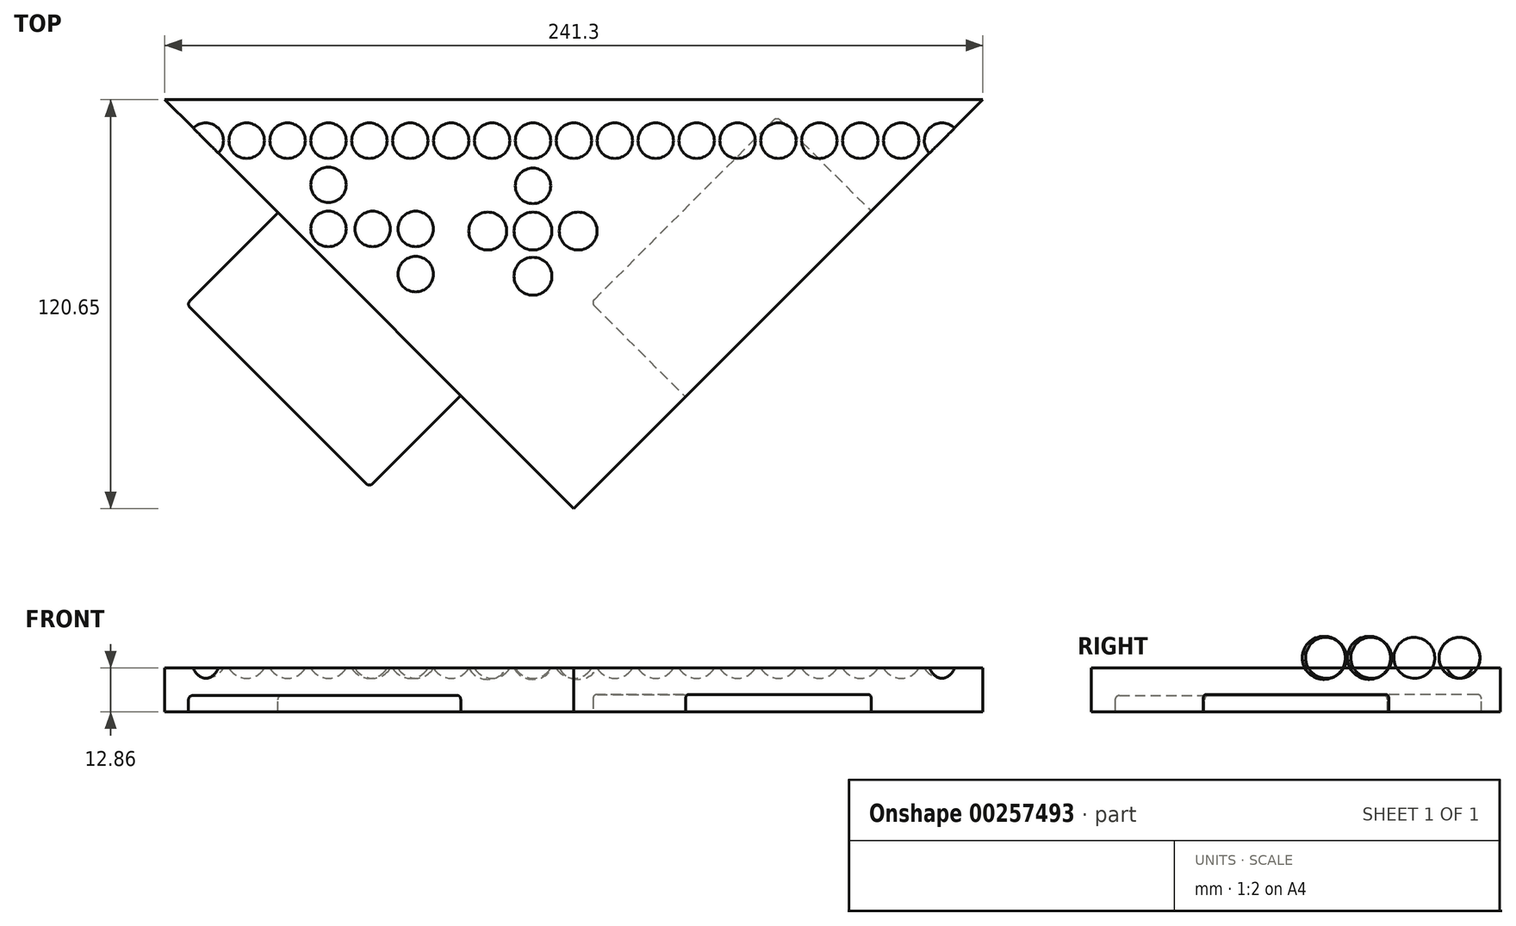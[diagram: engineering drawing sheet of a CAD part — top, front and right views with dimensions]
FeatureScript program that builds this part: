
annotation { "Feature Type Name" : "Feature", "Feature Type Description" : "" }
export const myFeature = defineFeature(function(context is Context, id is Id, definition is map)
    precondition{}
    {
        {
            var Q0;
            Q0=qCreatedBy(makeId("Top.planeOp"),FACE);
            var sketch = newSketch(context, id + "F0", { "sketchPlane" : qUnion([Q0])});
            skLineSegment(sketch, "E0.bottom", {"start": v(120.65, -120.65) * mm, "end": v(-120.65, -120.65) * mm});
            skLineSegment(sketch, "E0.top", {"start": v(120.65, 120.65) * mm, "end": v(-120.65, 120.65) * mm});
            skLineSegment(sketch, "E0.left", {"start": v(120.65, -120.65) * mm, "end": v(120.65, 120.65) * mm});
            skLineSegment(sketch, "E0.right", {"start": v(-120.65, -120.65) * mm, "end": v(-120.65, 120.65) * mm});
            skPoint(sketch, "E0.middle", {"position": v(0, 0) * mm});
            skSolve(sketch);
        }
        {
            var Q0;
            Q0=makeQuery(id+"F0.imprint","IMPRINT",FACE,{"disambiguationData":[TD([[makeQuery(id+"F0.imprint","IMPRINT",EDGE,{"derivedFrom":sQuery(id+"F0.wireOp",EDGE,"E0.bottom")}),-1.0]])]});
            extrude(context, id + "F1", {"entities" : qUnion([Q0]), "offsetDistance" : 25.4 * mm, "depth" : 12.7 * mm});
        }
        {
            var Q0;
            Q0=makeQuery(id+"F1.opExtrude","CAP_FACE",FACE,{"disambiguationData":[OSD([sQuery(id+"F0.wireOp",EDGE,"E0.bottom"),sQuery(id+"F0.wireOp",EDGE,"E0.top"),sQuery(id+"F0.wireOp",EDGE,"E0.left"),sQuery(id+"F0.wireOp",EDGE,"E0.right")])],"isStart":false});
            var sketch = newSketch(context, id + "F2", { "sketchPlane" : qUnion([Q0])});
            skLineSegment(sketch, "E1", {"start": v(120.65, 120.65) * mm, "end": v(0, 0) * mm});
            skLineSegment(sketch, "E2", {"start": v(0, 0) * mm, "end": v(-120.65, 120.65) * mm});
            skLineSegment(sketch, "E3", {"start": v(-120.65, 120.65) * mm, "end": v(-120.65, -120.65) * mm});
            skLineSegment(sketch, "E4", {"start": v(-120.65, -120.65) * mm, "end": v(120.65, -120.65) * mm});
            skLineSegment(sketch, "E5", {"start": v(120.65, -120.65) * mm, "end": v(120.65, 120.65) * mm});
            skSolve(sketch);
        }
        {
            var Q0;
            Q0 = qSketchRegion(id + "F2", true);
            extrude(context, id + "F3", {"entities" : qUnion([Q0]), "operationType" : NewBodyOperationType.REMOVE, "endBound" : BoundingType.THROUGH_ALL, "oppositeDirection" : true, "depth" : 25.4 * mm});
        }
        {
            var Q0;
            Q0=makeQuery(id+"F3.boolean.opBoolean","COPY",FACE,{"derivedFrom":makeQuery(id+"F3.opExtrude","SWEPT_FACE",FACE,{"disambiguationData":[OSD([sQuery(id+"F2.wireOp",EDGE,"E1")])]})});
            var sketch = newSketch(context, id + "F4", { "sketchPlane" : qUnion([Q0])});
            skLineSegment(sketch, "E6.bottom", {"start": v(124.05, 5.08) * mm, "end": v(46.58, 5.08) * mm});
            skLineSegment(sketch, "E6.top", {"start": v(124.05, -5.08) * mm, "end": v(46.58, -5.08) * mm});
            skLineSegment(sketch, "E6.left", {"start": v(124.05, 5.08) * mm, "end": v(124.05, -5.08) * mm});
            skLineSegment(sketch, "E6.right", {"start": v(46.58, 5.08) * mm, "end": v(46.58, -5.08) * mm});
            skPoint(sketch, "E6.middle", {"position": v(85.31, 0) * mm});
            skSolve(sketch);
        }
        {
            var Q0;
            Q0 = qSketchRegion(id + "F4", true);
            extrude(context, id + "F5", {"entities" : qUnion([Q0]), "operationType" : NewBodyOperationType.REMOVE, "oppositeDirection" : true, "depth" : 39.37 * mm});
        }
        {
            var Q0;
            Q0=makeQuery(id+"F3.boolean.opBoolean","COPY",FACE,{"derivedFrom":makeQuery(id+"F3.opExtrude","SWEPT_FACE",FACE,{"disambiguationData":[OSD([sQuery(id+"F2.wireOp",EDGE,"E2")])]})});
            var sketch = newSketch(context, id + "F6", { "sketchPlane" : qUnion([Q0])});
            skLineSegment(sketch, "E7.bottom", {"start": v(-47.21, -4.76) * mm, "end": v(-123.41, -4.76) * mm});
            skLineSegment(sketch, "E7.top", {"start": v(-47.21, 4.76) * mm, "end": v(-123.41, 4.76) * mm});
            skLineSegment(sketch, "E7.left", {"start": v(-47.21, -4.76) * mm, "end": v(-47.21, 4.76) * mm});
            skLineSegment(sketch, "E7.right", {"start": v(-123.41, -4.76) * mm, "end": v(-123.41, 4.76) * mm});
            skPoint(sketch, "E7.middle", {"position": v(-85.31, 0) * mm});
            skSolve(sketch);
        }
        {
            var Q0;
            {var subQ0=sQuery(id+"F6.wireOp",EDGE,"E7.top");Q0=makeQuery(id+"F6.imprint","IMPRINT",FACE,{"disambiguationData":[TD([[makeQuery(id+"F6.imprint","IMPRINT",EDGE,{"derivedFrom":subQ0}),1.0]])]});}
            extrude(context, id + "F7", {"entities" : qUnion([Q0]), "operationType" : NewBodyOperationType.ADD, "depth" : 38.1 * mm});
        }
        {
            var Q0;
            Q0=makeQuery(id+"F7.opExtrude","CAP_EDGE",EDGE,{"disambiguationData":[OSD([sQuery(id+"F6.wireOp",EDGE,"E7.left")])],"isStart":true});
            var Q1;
            Q1=makeQuery(id+"F7.opExtrude","CAP_EDGE",EDGE,{"disambiguationData":[OSD([sQuery(id+"F6.wireOp",EDGE,"E7.top")])],"isStart":true});
            var Q2;
            Q2=makeQuery(id+"F7.opExtrude","CAP_EDGE",EDGE,{"disambiguationData":[OSD([sQuery(id+"F6.wireOp",EDGE,"E7.right")])],"isStart":true});
            var Q3;
            Q3=makeQuery(id+"F5.boolean.opBoolean","COPY",EDGE,{"derivedFrom":makeQuery(id+"F5.opExtrude","CAP_EDGE",EDGE,{"disambiguationData":[OSD([sQuery(id+"F4.wireOp",EDGE,"E6.right")])],"isStart":false})});
            var Q4;
            Q4=makeQuery(id+"F5.boolean.opBoolean","COPY",EDGE,{"derivedFrom":makeQuery(id+"F5.opExtrude","CAP_EDGE",EDGE,{"disambiguationData":[OSD([sQuery(id+"F4.wireOp",EDGE,"E6.bottom")])],"isStart":false})});
            var Q5;
            Q5=makeQuery(id+"F5.boolean.opBoolean","COPY",EDGE,{"derivedFrom":makeQuery(id+"F5.opExtrude","CAP_EDGE",EDGE,{"disambiguationData":[OSD([sQuery(id+"F4.wireOp",EDGE,"E6.left")])],"isStart":false})});
            var Q6;
            Q6=makeQuery(id+"F5.boolean.opBoolean","COPY",EDGE,{"derivedFrom":makeQuery(id+"F5.opExtrude","SWEPT_EDGE",EDGE,{"disambiguationData":[OSD([sQuery(id+"F4.wireOp",EDGE,"E6.bottom"),sQuery(id+"F4.wireOp",EDGE,"E6.left")])]})});
            var Q7;
            Q7=makeQuery(id+"F5.boolean.opBoolean","COPY",EDGE,{"derivedFrom":makeQuery(id+"F5.opExtrude","SWEPT_EDGE",EDGE,{"disambiguationData":[OSD([sQuery(id+"F4.wireOp",EDGE,"E6.bottom"),sQuery(id+"F4.wireOp",EDGE,"E6.right")])]})});
            fillet(context, id + "F8", {"entities" : qUnion([Q0, Q1, Q2, Q3, Q4, Q5, Q6, Q7]), "radius" : 1.27 * mm, "tangentPropagation" : true, "allowEdgeOverflow" : false});
        }
        {
            var Q0;
            Q0=makeQuery(id+"F7.opExtrude","SWEPT_EDGE",EDGE,{"disambiguationData":[OSD([sQuery(id+"F6.wireOp",EDGE,"E7.top"),sQuery(id+"F6.wireOp",EDGE,"E7.left")])]});
            var Q1;
            Q1=makeQuery(id+"F7.opExtrude","CAP_EDGE",EDGE,{"disambiguationData":[OSD([sQuery(id+"F6.wireOp",EDGE,"E7.left")])],"isStart":false});
            var Q2;
            Q2=makeQuery(id+"F7.opExtrude","CAP_EDGE",EDGE,{"disambiguationData":[OSD([sQuery(id+"F6.wireOp",EDGE,"E7.top")])],"isStart":false});
            var Q3;
            Q3=makeQuery(id+"F7.opExtrude","CAP_EDGE",EDGE,{"disambiguationData":[OSD([sQuery(id+"F6.wireOp",EDGE,"E7.right")])],"isStart":false});
            var Q4;
            Q4=makeQuery(id+"F7.opExtrude","SWEPT_EDGE",EDGE,{"disambiguationData":[OSD([sQuery(id+"F6.wireOp",EDGE,"E7.top"),sQuery(id+"F6.wireOp",EDGE,"E7.right")])]});
            var Q5;
            Q5=makeQuery(id+"F5.boolean.opBoolean","COPY",EDGE,{"derivedFrom":makeQuery(id+"F5.opExtrude","CAP_EDGE",EDGE,{"disambiguationData":[OSD([sQuery(id+"F4.wireOp",EDGE,"E6.left")])],"isStart":true})});
            fillet(context, id + "F9", {"entities" : qUnion([Q0, Q1, Q2, Q3, Q4, Q5]), "radius" : 1.27 * mm, "tangentPropagation" : true, "allowEdgeOverflow" : false});
        }
        {
            var Q0;
            Q0=makeQuery(id+"F1.opExtrude","CAP_FACE",FACE,{"disambiguationData":[OSD([sQuery(id+"F0.wireOp",EDGE,"E0.bottom"),sQuery(id+"F0.wireOp",EDGE,"E0.top"),sQuery(id+"F0.wireOp",EDGE,"E0.left"),sQuery(id+"F0.wireOp",EDGE,"E0.right")])],"isStart":false});
            var sketch = newSketch(context, id + "F10", { "sketchPlane" : qUnion([Q0])});
            skLineSegment(sketch, "E8", {"start": v(-120.65, 120.65) * mm, "end": v(120.65, 120.65) * mm});
            skLineSegment(sketch, "E9", {"start": v(120.65, 120.65) * mm, "end": v(0, 0) * mm});
            skLineSegment(sketch, "E10", {"start": v(0, 0) * mm, "end": v(-120.65, 120.65) * mm});
            skSolve(sketch);
        }
        {
            var Q0;
            Q0 = qSketchRegion(id + "F10", true);
            extrude(context, id + "F11", {"entities" : qUnion([Q0]), "operationType" : NewBodyOperationType.ADD, "depth" : 3.17 * mm});
        }
        {
            var Q0;
            Q0=makeQuery(id+"F11.opExtrude","CAP_FACE",FACE,{"disambiguationData":[OSD([sQuery(id+"F10.wireOp",EDGE,"E8"),sQuery(id+"F10.wireOp",EDGE,"E9"),sQuery(id+"F10.wireOp",EDGE,"E10")])],"isStart":false});
            var sketch = newSketch(context, id + "F12", { "sketchPlane" : qUnion([Q0])});
            skCircle(sketch, "E11", {"center": v(0, 111.12) * mm, "radius": 6.35 * mm});
            skSolve(sketch);
        }
        {
            var Q0;
            Q0=makeQuery(id+"F12.imprint","IMPRINT",FACE,{"disambiguationData":[TD([[makeQuery(id+"F12.imprint","IMPRINT",EDGE,{"derivedFrom":sQuery(id+"F12.wireOp",EDGE,"E11")}),-1.0]])]});
            var sketch = newSketch(context, id + "F13", { "sketchPlane" : qUnion([Q0])});
            skLineSegment(sketch, "E12", {"start": v(0, 120.94) * mm, "end": v(0, 0) * mm});
            skSolve(sketch);
        }
        {
            var Q0;
            {var subQ0=makeQuery(id+"F12.imprint","IMPRINT",EDGE,{"derivedFrom":makeQuery(id+"F11.opExtrude","CAP_EDGE",EDGE,{"disambiguationData":[OSD([sQuery(id+"F10.wireOp",EDGE,"E9")])],"isStart":false})});Q0=makeQuery(id+"F13.imprint","IMPRINT",FACE,{"disambiguationData":[TD([[makeQuery(id+"F13.imprint","IMPRINT",EDGE,{"derivedFrom":subQ0}),-1.0]])]});}
            var sketch = newSketch(context, id + "F14", { "sketchPlane" : qUnion([Q0])});
            skArc(sketch, "E13", {"start": v(0, 114.59) * mm, "mid": v(6.03, 108.56) * mm, "end": v(0, 102.52) * mm});
            skLineSegment(sketch, "E14", {"start": v(0, 114.59) * mm, "end": v(0, 102.52) * mm});
            skSolve(sketch);
        }
        {
            var Q0;
            Q0 = qSketchRegion(id + "F14", true);
            var Q1;
            Q1=sQuery(id+"F14.wireOp",EDGE,"E14");
            revolve(context, id + "F15", {"operationType" : NewBodyOperationType.REMOVE, "entities" : qUnion([Q0]), "axis" : qUnion([Q1]), "revolveType" : RevolveType.FULL, "oppositeDirection" : true});
        }
        {
            var Q0;
            Q0=makeQuery(id+"F11.opExtrude","CAP_FACE",FACE,{"disambiguationData":[OSD([sQuery(id+"F10.wireOp",EDGE,"E8"),sQuery(id+"F10.wireOp",EDGE,"E9"),sQuery(id+"F10.wireOp",EDGE,"E10")])],"isStart":false});
            var sketch = newSketch(context, id + "F16", { "sketchPlane" : qUnion([Q0])});
            skLineSegment(sketch, "E15", {"start": v(0, 108.56) * mm, "end": v(-6.03, 108.56) * mm});
            skLineSegment(sketch, "E16", {"start": v(-6.03, 108.56) * mm, "end": v(-18.1, 108.56) * mm});
            skArc(sketch, "E17", {"start": v(-18.1, 108.56) * mm, "mid": v(-12.07, 114.59) * mm, "end": v(-6.03, 108.56) * mm});
            skSolve(sketch);
        }
        {
            var Q0;
            Q0=makeQuery(id+"F16.imprint","IMPRINT",FACE,{"disambiguationData":[TD([[makeQuery(id+"F16.imprint","IMPRINT",EDGE,{"derivedFrom":sQuery(id+"F16.wireOp",EDGE,"E16")}),-1.0]])]});
            var Q1;
            Q1=sQuery(id+"F16.wireOp",EDGE,"E16");
            revolve(context, id + "F17", {"operationType" : NewBodyOperationType.REMOVE, "entities" : qUnion([Q0]), "axis" : qUnion([Q1]), "revolveType" : RevolveType.FULL, "oppositeDirection" : true});
        }
        {
            var Q0;
            Q0=makeQuery(id+"F11.opExtrude","CAP_FACE",FACE,{"disambiguationData":[OSD([sQuery(id+"F10.wireOp",EDGE,"E8"),sQuery(id+"F10.wireOp",EDGE,"E9"),sQuery(id+"F10.wireOp",EDGE,"E10")])],"isStart":false});
            var sketch = newSketch(context, id + "F18", { "sketchPlane" : qUnion([Q0])});
            skLineSegment(sketch, "E18", {"start": v(-11.75, 108.56) * mm, "end": v(-18.1, 108.56) * mm});
            skLineSegment(sketch, "E19", {"start": v(-18.1, 108.56) * mm, "end": v(-30.16, 108.56) * mm});
            skArc(sketch, "E20", {"start": v(-30.16, 108.56) * mm, "mid": v(-24.13, 114.59) * mm, "end": v(-18.1, 108.56) * mm});
            skSolve(sketch);
        }
        {
            var Q0;
            Q0=makeQuery(id+"F16.imprint","IMPRINT",FACE,{"disambiguationData":[TD([[makeQuery(id+"F16.imprint","IMPRINT",EDGE,{"derivedFrom":sQuery(id+"F16.wireOp",EDGE,"E16")}),1.0]])]});
            var sketch = newSketch(context, id + "F19", { "sketchPlane" : qUnion([Q0])});
            skLineSegment(sketch, "E21", {"start": v(-30.16, 108.56) * mm, "end": v(-42.23, 108.56) * mm});
            skArc(sketch, "E22", {"start": v(-42.23, 108.56) * mm, "mid": v(-36.2, 114.59) * mm, "end": v(-30.16, 108.56) * mm});
            skSolve(sketch);
        }
        {
            var Q0;
            Q0 = qSketchRegion(id + "F18", true);
            var Q1;
            Q1 = qSketchRegion(id + "F19", true);
            var Q2;
            Q2=sQuery(id+"F19.wireOp",EDGE,"E21");
            revolve(context, id + "F20", {"operationType" : NewBodyOperationType.REMOVE, "entities" : qUnion([Q0, Q1]), "axis" : qUnion([Q2]), "revolveType" : RevolveType.FULL, "oppositeDirection" : true});
        }
        {
            var Q0;
            Q0=makeQuery(id+"F16.imprint","IMPRINT",FACE,{"disambiguationData":[TD([[makeQuery(id+"F16.imprint","IMPRINT",EDGE,{"derivedFrom":sQuery(id+"F16.wireOp",EDGE,"E16")}),1.0]])]});
            var sketch = newSketch(context, id + "F21", { "sketchPlane" : qUnion([Q0])});
            skLineSegment(sketch, "E23", {"start": v(-42.23, 108.56) * mm, "end": v(-54.3, 108.56) * mm});
            skArc(sketch, "E24", {"start": v(-54.3, 108.56) * mm, "mid": v(-48.26, 114.59) * mm, "end": v(-42.23, 108.56) * mm});
            skSolve(sketch);
        }
        {
            var Q0;
            Q0=makeQuery(id+"F16.imprint","IMPRINT",FACE,{"disambiguationData":[TD([[makeQuery(id+"F16.imprint","IMPRINT",EDGE,{"derivedFrom":sQuery(id+"F16.wireOp",EDGE,"E16")}),1.0]])]});
            var sketch = newSketch(context, id + "F22", { "sketchPlane" : qUnion([Q0])});
            skLineSegment(sketch, "E25", {"start": v(-54.3, 108.56) * mm, "end": v(-66.36, 108.56) * mm});
            skArc(sketch, "E26", {"start": v(-66.36, 108.56) * mm, "mid": v(-60.32, 114.59) * mm, "end": v(-54.3, 108.56) * mm});
            skSolve(sketch);
        }
        {
            var Q0;
            Q0=makeQuery(id+"F16.imprint","IMPRINT",FACE,{"disambiguationData":[TD([[makeQuery(id+"F16.imprint","IMPRINT",EDGE,{"derivedFrom":sQuery(id+"F16.wireOp",EDGE,"E16")}),1.0]])]});
            var sketch = newSketch(context, id + "F23", { "sketchPlane" : qUnion([Q0])});
            skLineSegment(sketch, "E27", {"start": v(-66.36, 108.56) * mm, "end": v(-78.42, 108.56) * mm});
            skArc(sketch, "E28", {"start": v(-78.42, 108.56) * mm, "mid": v(-72.4, 114.59) * mm, "end": v(-66.36, 108.56) * mm});
            skSolve(sketch);
        }
        {
            var Q0;
            Q0=makeQuery(id+"F19.imprint","IMPRINT",FACE,{"disambiguationData":[TD([[makeQuery(id+"F19.imprint","IMPRINT",EDGE,{"derivedFrom":sQuery(id+"F19.wireOp",EDGE,"E21")}),1.0]])]});
            var sketch = newSketch(context, id + "F24", { "sketchPlane" : qUnion([Q0])});
            skLineSegment(sketch, "E29", {"start": v(-78.42, 108.56) * mm, "end": v(-90.49, 108.56) * mm});
            skArc(sketch, "E30", {"start": v(-90.49, 108.56) * mm, "mid": v(-84.46, 114.59) * mm, "end": v(-78.42, 108.56) * mm});
            skSolve(sketch);
        }
        {
            var Q0;
            {var subQ0=makeQuery(id+"F12.imprint","IMPRINT",EDGE,{"derivedFrom":makeQuery(id+"F11.opExtrude","CAP_EDGE",EDGE,{"disambiguationData":[OSD([sQuery(id+"F10.wireOp",EDGE,"E9")])],"isStart":false})});Q0=makeQuery(id+"F14.imprint","IMPRINT",FACE,{"disambiguationData":[TD([[makeQuery(id+"F14.imprint","IMPRINT",EDGE,{"derivedFrom":makeQuery(id+"F13.imprint","IMPRINT",EDGE,{"derivedFrom":subQ0})}),-1.0]])]});}
            var sketch = newSketch(context, id + "F25", { "sketchPlane" : qUnion([Q0])});
            skLineSegment(sketch, "E31", {"start": v(-90.49, 108.56) * mm, "end": v(-102.55, 108.56) * mm});
            skArc(sketch, "E32", {"start": v(-102.55, 108.56) * mm, "mid": v(-96.52, 114.59) * mm, "end": v(-90.49, 108.56) * mm});
            skSolve(sketch);
        }
        {
            var Q0;
            Q0=makeQuery(id+"F24.imprint","IMPRINT",FACE,{"disambiguationData":[TD([[makeQuery(id+"F24.imprint","IMPRINT",EDGE,{"derivedFrom":sQuery(id+"F24.wireOp",EDGE,"E29")}),1.0]])]});
            var sketch = newSketch(context, id + "F26", { "sketchPlane" : qUnion([Q0])});
            skLineSegment(sketch, "E33", {"start": v(-102.55, 108.56) * mm, "end": v(-114.62, 108.56) * mm});
            skArc(sketch, "E34", {"start": v(-114.62, 108.56) * mm, "mid": v(-108.59, 114.59) * mm, "end": v(-102.55, 108.56) * mm});
            skSolve(sketch);
        }
        {
            var Q0;
            Q0 = qSketchRegion(id + "F21", true);
            var Q1;
            Q1 = qSketchRegion(id + "F22", true);
            var Q2;
            Q2 = qSketchRegion(id + "F23", true);
            var Q3;
            Q3 = qSketchRegion(id + "F24", true);
            var Q4;
            Q4 = qSketchRegion(id + "F25", true);
            var Q5;
            Q5 = qSketchRegion(id + "F26", true);
            var Q6;
            Q6=sQuery(id+"F21.wireOp",EDGE,"E23");
            revolve(context, id + "F27", {"operationType" : NewBodyOperationType.REMOVE, "entities" : qUnion([Q0, Q1, Q2, Q3, Q4, Q5]), "axis" : qUnion([Q6]), "revolveType" : RevolveType.FULL, "oppositeDirection" : true});
        }
        {
            var Q0;
            Q0=makeQuery(id+"F19.imprint","IMPRINT",FACE,{"disambiguationData":[TD([[makeQuery(id+"F19.imprint","IMPRINT",EDGE,{"derivedFrom":sQuery(id+"F19.wireOp",EDGE,"E21")}),1.0]])]});
            var sketch = newSketch(context, id + "F28", { "sketchPlane" : qUnion([Q0])});
            skLineSegment(sketch, "E35", {"start": v(6.03, 108.56) * mm, "end": v(18.1, 108.56) * mm});
            skArc(sketch, "E36", {"start": v(6.03, 108.56) * mm, "mid": v(12.07, 114.59) * mm, "end": v(18.1, 108.56) * mm});
            skSolve(sketch);
        }
        {
            var Q0;
            Q0=makeQuery(id+"F19.imprint","IMPRINT",FACE,{"disambiguationData":[TD([[makeQuery(id+"F19.imprint","IMPRINT",EDGE,{"derivedFrom":sQuery(id+"F19.wireOp",EDGE,"E21")}),1.0]])]});
            var sketch = newSketch(context, id + "F29", { "sketchPlane" : qUnion([Q0])});
            skLineSegment(sketch, "E37", {"start": v(18.1, 108.56) * mm, "end": v(30.16, 108.56) * mm});
            skArc(sketch, "E38", {"start": v(18.1, 108.56) * mm, "mid": v(24.13, 114.59) * mm, "end": v(30.16, 108.56) * mm});
            skSolve(sketch);
        }
        {
            var Q0;
            Q0=makeQuery(id+"F19.imprint","IMPRINT",FACE,{"disambiguationData":[TD([[makeQuery(id+"F19.imprint","IMPRINT",EDGE,{"derivedFrom":sQuery(id+"F19.wireOp",EDGE,"E21")}),1.0]])]});
            var sketch = newSketch(context, id + "F30", { "sketchPlane" : qUnion([Q0])});
            skLineSegment(sketch, "E39", {"start": v(42.23, 108.56) * mm, "end": v(30.16, 108.56) * mm});
            skArc(sketch, "E40", {"start": v(30.16, 108.56) * mm, "mid": v(36.2, 114.59) * mm, "end": v(42.23, 108.56) * mm});
            skSolve(sketch);
        }
        {
            var Q0;
            Q0=makeQuery(id+"F19.imprint","IMPRINT",FACE,{"disambiguationData":[TD([[makeQuery(id+"F19.imprint","IMPRINT",EDGE,{"derivedFrom":sQuery(id+"F19.wireOp",EDGE,"E21")}),1.0]])]});
            var sketch = newSketch(context, id + "F31", { "sketchPlane" : qUnion([Q0])});
            skLineSegment(sketch, "E41", {"start": v(42.23, 108.56) * mm, "end": v(54.3, 108.56) * mm});
            skArc(sketch, "E42", {"start": v(42.23, 108.56) * mm, "mid": v(48.26, 114.59) * mm, "end": v(54.3, 108.56) * mm});
            skSolve(sketch);
        }
        {
            var Q0;
            Q0=makeQuery(id+"F19.imprint","IMPRINT",FACE,{"disambiguationData":[TD([[makeQuery(id+"F19.imprint","IMPRINT",EDGE,{"derivedFrom":sQuery(id+"F19.wireOp",EDGE,"E21")}),1.0]])]});
            var sketch = newSketch(context, id + "F32", { "sketchPlane" : qUnion([Q0])});
            skLineSegment(sketch, "E43", {"start": v(66.36, 108.56) * mm, "end": v(54.3, 108.56) * mm});
            skArc(sketch, "E44", {"start": v(54.3, 108.56) * mm, "mid": v(60.33, 114.59) * mm, "end": v(66.36, 108.56) * mm});
            skSolve(sketch);
        }
        {
            var Q0;
            Q0=makeQuery(id+"F19.imprint","IMPRINT",FACE,{"disambiguationData":[TD([[makeQuery(id+"F19.imprint","IMPRINT",EDGE,{"derivedFrom":sQuery(id+"F19.wireOp",EDGE,"E21")}),1.0]])]});
            var sketch = newSketch(context, id + "F33", { "sketchPlane" : qUnion([Q0])});
            skLineSegment(sketch, "E45", {"start": v(78.42, 108.56) * mm, "end": v(66.36, 108.56) * mm});
            skArc(sketch, "E46", {"start": v(66.36, 108.56) * mm, "mid": v(72.4, 114.59) * mm, "end": v(78.42, 108.56) * mm});
            skSolve(sketch);
        }
        {
            var Q0;
            Q0=makeQuery(id+"F19.imprint","IMPRINT",FACE,{"disambiguationData":[TD([[makeQuery(id+"F19.imprint","IMPRINT",EDGE,{"derivedFrom":sQuery(id+"F19.wireOp",EDGE,"E21")}),1.0]])]});
            var sketch = newSketch(context, id + "F34", { "sketchPlane" : qUnion([Q0])});
            skLineSegment(sketch, "E47", {"start": v(90.49, 108.56) * mm, "end": v(78.42, 108.56) * mm});
            skArc(sketch, "E48", {"start": v(78.42, 108.56) * mm, "mid": v(84.45, 114.59) * mm, "end": v(90.49, 108.56) * mm});
            skSolve(sketch);
        }
        {
            var Q0;
            Q0=makeQuery(id+"F19.imprint","IMPRINT",FACE,{"disambiguationData":[TD([[makeQuery(id+"F19.imprint","IMPRINT",EDGE,{"derivedFrom":sQuery(id+"F19.wireOp",EDGE,"E21")}),1.0]])]});
            var sketch = newSketch(context, id + "F35", { "sketchPlane" : qUnion([Q0])});
            skLineSegment(sketch, "E49", {"start": v(102.55, 108.56) * mm, "end": v(90.49, 108.56) * mm});
            skArc(sketch, "E50", {"start": v(90.49, 108.56) * mm, "mid": v(96.52, 114.59) * mm, "end": v(102.55, 108.56) * mm});
            skSolve(sketch);
        }
        {
            var Q0;
            Q0=makeQuery(id+"F19.imprint","IMPRINT",FACE,{"disambiguationData":[TD([[makeQuery(id+"F19.imprint","IMPRINT",EDGE,{"derivedFrom":sQuery(id+"F19.wireOp",EDGE,"E21")}),1.0]])]});
            var sketch = newSketch(context, id + "F36", { "sketchPlane" : qUnion([Q0])});
            skLineSegment(sketch, "E51", {"start": v(114.62, 108.56) * mm, "end": v(102.55, 108.56) * mm});
            skArc(sketch, "E52", {"start": v(102.55, 108.56) * mm, "mid": v(108.58, 114.59) * mm, "end": v(114.62, 108.56) * mm});
            skSolve(sketch);
        }
        {
            var Q0;
            Q0 = qSketchRegion(id + "F28", true);
            var Q1;
            Q1 = qSketchRegion(id + "F29", true);
            var Q2;
            Q2 = qSketchRegion(id + "F30", true);
            var Q3;
            Q3 = qSketchRegion(id + "F31", true);
            var Q4;
            Q4 = qSketchRegion(id + "F32", true);
            var Q5;
            Q5 = qSketchRegion(id + "F33", true);
            var Q6;
            Q6 = qSketchRegion(id + "F34", true);
            var Q7;
            Q7 = qSketchRegion(id + "F35", true);
            var Q8;
            Q8 = qSketchRegion(id + "F36", true);
            var Q9;
            Q9=sQuery(id+"F28.wireOp",EDGE,"E35");
            revolve(context, id + "F37", {"operationType" : NewBodyOperationType.REMOVE, "entities" : qUnion([Q0, Q1, Q2, Q3, Q4, Q5, Q6, Q7, Q8]), "axis" : qUnion([Q9]), "revolveType" : RevolveType.FULL, "oppositeDirection" : true});
        }
        {
            var Q0;
            Q0=makeQuery(id+"F11.boolean.opBoolean","MERGE",FACE,{"derivedFrom":[makeQuery(id+"F1.opExtrude","SWEPT_FACE",FACE,{"disambiguationData":[OSD([sQuery(id+"F0.wireOp",EDGE,"E0.top")])]}),makeQuery(id+"F11.opExtrude","SWEPT_FACE",FACE,{"disambiguationData":[OSD([sQuery(id+"F10.wireOp",EDGE,"E8")])]})]});
            var sketch = newSketch(context, id + "F38", { "sketchPlane" : qUnion([Q0])});
            skLineSegment(sketch, "E53.bottom", {"start": v(-146.05, 12.86) * mm, "end": v(158.75, 12.86) * mm});
            skLineSegment(sketch, "E53.top", {"start": v(-146.05, 27.73) * mm, "end": v(158.75, 27.73) * mm});
            skLineSegment(sketch, "E53.left", {"start": v(-146.05, 12.86) * mm, "end": v(-146.05, 27.73) * mm});
            skLineSegment(sketch, "E53.right", {"start": v(158.75, 12.86) * mm, "end": v(158.75, 27.73) * mm});
            skSolve(sketch);
        }
        {
            var Q0;
            Q0=makeQuery(id+"F23.imprint","IMPRINT",FACE,{"disambiguationData":[TD([[makeQuery(id+"F23.imprint","IMPRINT",EDGE,{"derivedFrom":sQuery(id+"F23.wireOp",EDGE,"E27")}),1.0]])]});
            var sketch = newSketch(context, id + "F39", { "sketchPlane" : qUnion([Q0])});
            skLineSegment(sketch, "E54", {"start": v(-72.4, 101.57) * mm, "end": v(-72.4, 89.5) * mm});
            skArc(sketch, "E55", {"start": v(-72.4, 89.5) * mm, "mid": v(-66.36, 95.54) * mm, "end": v(-72.4, 101.57) * mm});
            skSolve(sketch);
        }
        {
            var Q0;
            Q0=makeQuery(id+"F23.imprint","IMPRINT",FACE,{"disambiguationData":[TD([[makeQuery(id+"F23.imprint","IMPRINT",EDGE,{"derivedFrom":sQuery(id+"F23.wireOp",EDGE,"E27")}),1.0]])]});
            var sketch = newSketch(context, id + "F40", { "sketchPlane" : qUnion([Q0])});
            skLineSegment(sketch, "E56", {"start": v(-72.4, 88.55) * mm, "end": v(-72.4, 76.49) * mm});
            skArc(sketch, "E57", {"start": v(-72.4, 76.49) * mm, "mid": v(-66.36, 82.52) * mm, "end": v(-72.4, 88.55) * mm});
            skSolve(sketch);
        }
        {
            var Q0;
            Q0 = qSketchRegion(id + "F39", true);
            var Q1;
            Q1 = qSketchRegion(id + "F40", true);
            var Q2;
            Q2=sQuery(id+"F39.wireOp",EDGE,"E54");
            revolve(context, id + "F41", {"operationType" : NewBodyOperationType.REMOVE, "entities" : qUnion([Q0, Q1]), "axis" : qUnion([Q2]), "revolveType" : RevolveType.FULL, "oppositeDirection" : true});
        }
        {
            var Q0;
            Q0=makeQuery(id+"F23.imprint","IMPRINT",FACE,{"disambiguationData":[TD([[makeQuery(id+"F23.imprint","IMPRINT",EDGE,{"derivedFrom":sQuery(id+"F23.wireOp",EDGE,"E27")}),1.0]])]});
            var sketch = newSketch(context, id + "F42", { "sketchPlane" : qUnion([Q0])});
            skLineSegment(sketch, "E58", {"start": v(-65.4, 82.52) * mm, "end": v(-53.34, 82.52) * mm});
            skArc(sketch, "E59", {"start": v(-65.4, 82.52) * mm, "mid": v(-59.37, 76.49) * mm, "end": v(-53.34, 82.52) * mm});
            skSolve(sketch);
        }
        {
            var Q0;
            Q0=makeQuery(id+"F23.imprint","IMPRINT",FACE,{"disambiguationData":[TD([[makeQuery(id+"F23.imprint","IMPRINT",EDGE,{"derivedFrom":sQuery(id+"F23.wireOp",EDGE,"E27")}),1.0]])]});
            var sketch = newSketch(context, id + "F43", { "sketchPlane" : qUnion([Q0])});
            skLineSegment(sketch, "E60", {"start": v(-52.7, 82.52) * mm, "end": v(-40.64, 82.52) * mm});
            skArc(sketch, "E61", {"start": v(-52.7, 82.52) * mm, "mid": v(-46.67, 88.55) * mm, "end": v(-40.64, 82.52) * mm});
            skSolve(sketch);
        }
        {
            var Q0;
            Q0=makeQuery(id+"F23.imprint","IMPRINT",FACE,{"disambiguationData":[TD([[makeQuery(id+"F23.imprint","IMPRINT",EDGE,{"derivedFrom":sQuery(id+"F23.wireOp",EDGE,"E27")}),1.0]])]});
            var sketch = newSketch(context, id + "F44", { "sketchPlane" : qUnion([Q0])});
            skLineSegment(sketch, "E62", {"start": v(-52.7, 69.19) * mm, "end": v(-40.64, 69.19) * mm});
            skArc(sketch, "E63", {"start": v(-52.7, 69.19) * mm, "mid": v(-46.67, 75.22) * mm, "end": v(-40.64, 69.19) * mm});
            skSolve(sketch);
        }
        {
            var Q0;
            Q0 = qSketchRegion(id + "F42", true);
            var Q1;
            Q1 = qSketchRegion(id + "F43", true);
            var Q2;
            Q2=sQuery(id+"F42.wireOp",EDGE,"E58");
            revolve(context, id + "F45", {"operationType" : NewBodyOperationType.REMOVE, "entities" : qUnion([Q0, Q1]), "axis" : qUnion([Q2]), "revolveType" : RevolveType.FULL, "oppositeDirection" : true});
        }
        {
            var Q0;
            Q0 = qSketchRegion(id + "F44", true);
            var Q1;
            Q1=sQuery(id+"F44.wireOp",EDGE,"E62");
            revolve(context, id + "F46", {"operationType" : NewBodyOperationType.REMOVE, "entities" : qUnion([Q0]), "axis" : qUnion([Q1]), "revolveType" : RevolveType.FULL, "oppositeDirection" : true});
        }
        {
            var Q0;
            Q0=makeQuery(id+"F23.imprint","IMPRINT",FACE,{"disambiguationData":[TD([[makeQuery(id+"F23.imprint","IMPRINT",EDGE,{"derivedFrom":sQuery(id+"F23.wireOp",EDGE,"E27")}),1.0]])]});
            var sketch = newSketch(context, id + "F47", { "sketchPlane" : qUnion([Q0])});
            skLineSegment(sketch, "E64", {"start": v(-6.03, 95.22) * mm, "end": v(-18.1, 95.22) * mm});
            skArc(sketch, "E65", {"start": v(-18.1, 95.22) * mm, "mid": v(-12.07, 101.25) * mm, "end": v(-6.03, 95.22) * mm});
            skSolve(sketch);
        }
        {
            var Q0;
            Q0=makeQuery(id+"F16.imprint","IMPRINT",FACE,{"disambiguationData":[TD([[makeQuery(id+"F16.imprint","IMPRINT",EDGE,{"derivedFrom":sQuery(id+"F16.wireOp",EDGE,"E16")}),1.0]])]});
            var sketch = newSketch(context, id + "F48", { "sketchPlane" : qUnion([Q0])});
            skLineSegment(sketch, "E66", {"start": v(-18.42, 81.89) * mm, "end": v(-5.72, 81.89) * mm});
            skArc(sketch, "E67", {"start": v(-18.42, 81.89) * mm, "mid": v(-12.07, 88.24) * mm, "end": v(-5.72, 81.89) * mm});
            skSolve(sketch);
        }
        {
            var Q0;
            Q0=makeQuery(id+"F16.imprint","IMPRINT",FACE,{"disambiguationData":[TD([[makeQuery(id+"F16.imprint","IMPRINT",EDGE,{"derivedFrom":sQuery(id+"F16.wireOp",EDGE,"E16")}),1.0]])]});
            var sketch = newSketch(context, id + "F49", { "sketchPlane" : qUnion([Q0])});
            skLineSegment(sketch, "E68", {"start": v(-18.42, 68.55) * mm, "end": v(-5.72, 68.55) * mm});
            skArc(sketch, "E69", {"start": v(-5.72, 68.55) * mm, "mid": v(-12.07, 74.9) * mm, "end": v(-18.42, 68.55) * mm});
            skSolve(sketch);
        }
        {
            var Q0;
            Q0=makeQuery(id+"F16.imprint","IMPRINT",FACE,{"disambiguationData":[TD([[makeQuery(id+"F16.imprint","IMPRINT",EDGE,{"derivedFrom":sQuery(id+"F16.wireOp",EDGE,"E16")}),1.0]])]});
            var sketch = newSketch(context, id + "F50", { "sketchPlane" : qUnion([Q0])});
            skLineSegment(sketch, "E70", {"start": v(-5.08, 81.89) * mm, "end": v(7.62, 81.89) * mm});
            skArc(sketch, "E71", {"start": v(-5.08, 81.89) * mm, "mid": v(1.27, 88.24) * mm, "end": v(7.62, 81.89) * mm});
            skSolve(sketch);
        }
        {
            var Q0;
            Q0=makeQuery(id+"F16.imprint","IMPRINT",FACE,{"disambiguationData":[TD([[makeQuery(id+"F16.imprint","IMPRINT",EDGE,{"derivedFrom":sQuery(id+"F16.wireOp",EDGE,"E16")}),1.0]])]});
            var sketch = newSketch(context, id + "F51", { "sketchPlane" : qUnion([Q0])});
            skLineSegment(sketch, "E72", {"start": v(-19.05, 81.89) * mm, "end": v(-31.75, 81.89) * mm});
            skArc(sketch, "E73", {"start": v(-31.75, 81.89) * mm, "mid": v(-25.4, 88.24) * mm, "end": v(-19.05, 81.89) * mm});
            skSolve(sketch);
        }
        {
            var Q0;
            Q0 = qSketchRegion(id + "F51", true);
            var Q1;
            Q1 = qSketchRegion(id + "F50", true);
            var Q2;
            Q2 = qSketchRegion(id + "F48", true);
            var Q3;
            Q3=sQuery(id+"F50.wireOp",EDGE,"E70");
            revolve(context, id + "F52", {"operationType" : NewBodyOperationType.REMOVE, "entities" : qUnion([Q0, Q1, Q2]), "axis" : qUnion([Q3]), "revolveType" : RevolveType.FULL, "oppositeDirection" : true});
        }
        {
            var Q0;
            Q0 = qSketchRegion(id + "F47", true);
            var Q1;
            Q1=sQuery(id+"F47.wireOp",EDGE,"E64");
            revolve(context, id + "F53", {"operationType" : NewBodyOperationType.REMOVE, "entities" : qUnion([Q0]), "axis" : qUnion([Q1]), "revolveType" : RevolveType.FULL, "oppositeDirection" : true});
        }
        {
            var Q0;
            Q0 = qSketchRegion(id + "F49", true);
            var Q1;
            Q1=sQuery(id+"F49.wireOp",EDGE,"E68");
            revolve(context, id + "F54", {"operationType" : NewBodyOperationType.REMOVE, "entities" : qUnion([Q0]), "axis" : qUnion([Q1]), "revolveType" : RevolveType.FULL, "oppositeDirection" : true});
        }
        {
            var Q0;
            Q0 = qSketchRegion(id + "F38", true);
            extrude(context, id + "F55", {"entities" : qUnion([Q0]), "operationType" : NewBodyOperationType.REMOVE, "endBound" : BoundingType.THROUGH_ALL, "oppositeDirection" : true, "depth" : 25.4 * mm});
        }
    });
